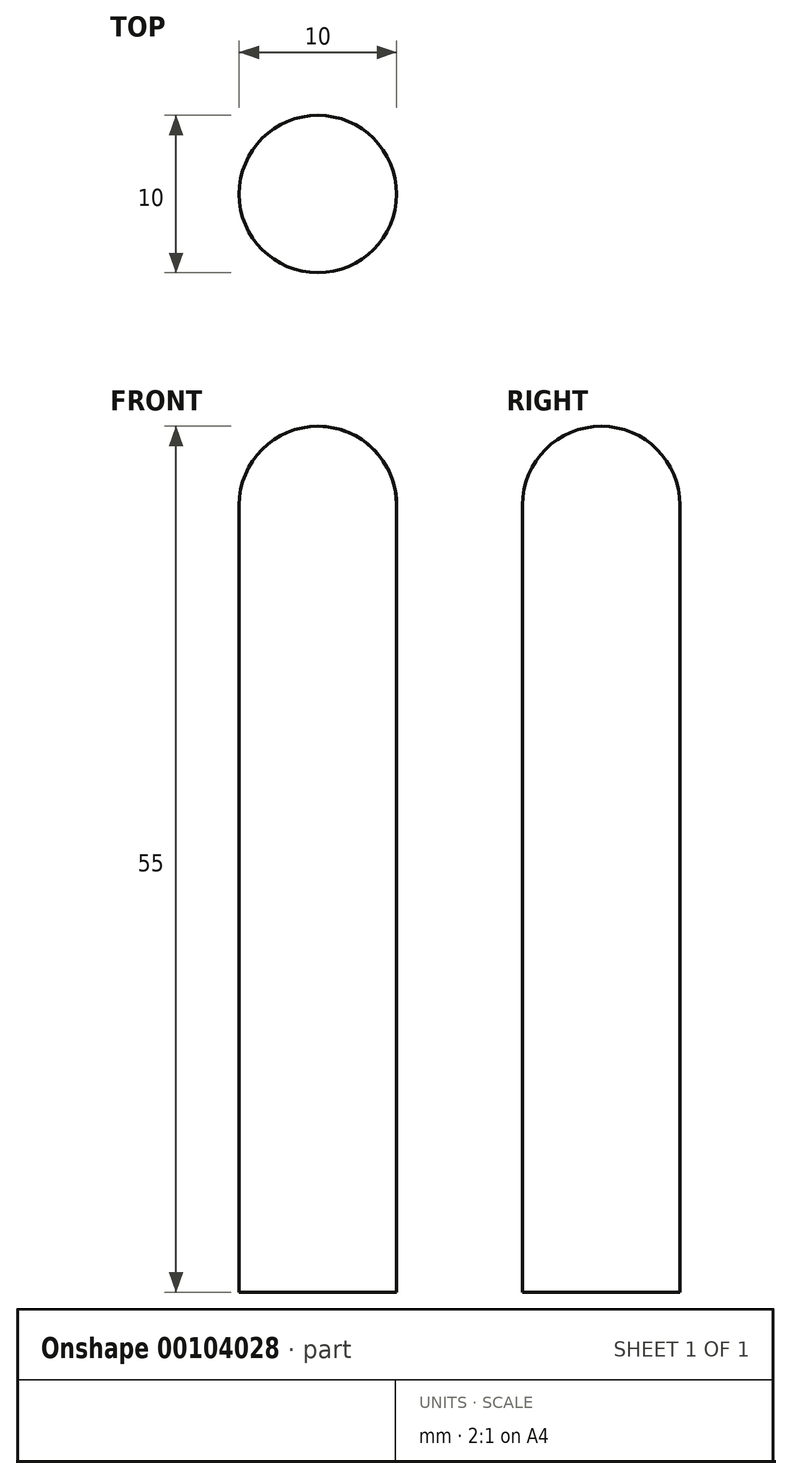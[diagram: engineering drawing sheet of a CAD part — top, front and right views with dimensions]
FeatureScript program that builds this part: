
annotation { "Feature Type Name" : "Feature", "Feature Type Description" : "" }
export const myFeature = defineFeature(function(context is Context, id is Id, definition is map)
    precondition{}
    {
        {
            var Q0;
            Q0=qCreatedBy(makeId("Top.planeOp"),FACE);
            var sketch = newSketch(context, id + "F0", { "sketchPlane" : qUnion([Q0])});
            skCircle(sketch, "E0", {"center": v(0, 0) * mm, "radius": 5 * mm});
            skSolve(sketch);
        }
        {
            var Q0;
            Q0 = qSketchRegion(id + "F0", true);
            extrude(context, id + "F1", {"entities" : qUnion([Q0]), "depth" : 55 * mm, "offsetDistance" : 25 * mm});
        }
        {
            var Q0;
            Q0=makeQuery(id+"F1.opExtrude","CAP_EDGE",EDGE,{"disambiguationData":[OSD([sQuery(id+"F0.wireOp",EDGE,"E0")])],"isStart":false});
            fillet(context, id + "F2", {"entities" : qUnion([Q0]), "tangentPropagation" : true, "radius" : 5 * mm, "defaultsChanged" : false, "vertexSettings" : [], "allowEdgeOverflow" : false});
        }
    });
